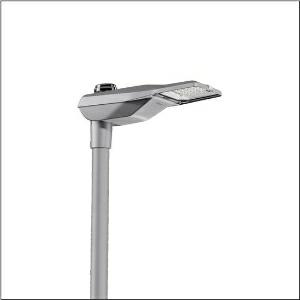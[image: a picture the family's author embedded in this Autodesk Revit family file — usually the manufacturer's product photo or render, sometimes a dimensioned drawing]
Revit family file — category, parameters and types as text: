
# Revit family: streetlight_sl_21_micro___st0_8a_5xe5c47n08cb_5e3b
name_source: partatom
category: Lighting Fixtures
units: mm (PartAtom-declared; Revit-internal decimal feet)

## family parameters
Cut with Voids When Loaded = No
Host = Face
Light Source = No
Part Type = Normal
Room Calculation Point = No
Round Connector Dimension = Use Diameter
Shared = No

## types (1)
- --- (1 x LED, 2380 lm, 15.8 W, 4000K)
    Apparent Load = 16 VA
    CIE Flux Codes = 38 75 97 100 100
    Color Rendering = 70
    Color Temperature = 4000K
    Default Elevation = 1800 mm
    Description = Streetlight SL 21 micro, mast luminaire, primary light control with lens, of PMMA, primary optical cover: cover, of toughened safety glass, transparent, light distribution: ST0.8a, light emission: direct distribution, primary light characteristic: asymmetric, installation type: post-top, LED, 3G 1.5mm², High Power LED, rated luminous flux: 2.380lm, luminous efficacy: 151lm/W, light colour: 740, colour temperature: 4000K, control gear: NEMA (7pin), control: overheat protection, pre-setting: linear dimming characteristic, constant luminous flux control, time-dependent luminous flux control, flexible luminous flux parameterisation, mains connection: 230..240V, AC, 50/60Hz, connection cable pre-assembled, cable length: 6,5m, wiring characteristics: H07RN-F, start of lifetime: 16W, end of service life: 16W, reduction: 8W, luminaire housing, of diecast aluminium (EN AC-44300), powder-coated, SITECO metallic grey (DB 702S), corrosivity category C5 high according to DIN EN ISO 12944, multi-level sealing system, sealing non-destructively replaceable, inclination adjustable: 0°, 5°, 10°, 15°, length: 528mm, width: 235mm, height: 110mm, spigot size: 76/60mm (post-top), mounting height: 4..8m, protection rating (complete): IP66, insulation class (complete): insulation class I (protective earthing), certification: CE, ENEC, ENEC+, VDE, impact resistance: IK10, permissible operating ambient temperature for outdoor applications: -40..+50°C, standard-compliant lighting for roads and squares, packaging unit: 1 piece

Light Distribution: ST0.8a
    Height = 110 mm
    Lamp = 1 x LED
    Lamp Light Flux = 2380 lm
    Lamp Power = 15.8 W
    Lamp count = 1
    Length = 528 mm
    Luminous efficacy = 151 lm/W
    Manufacturer = Siteco
    ModVariant = No
    Model = 5XE5C47N08CB
    Number of Poles = 1
    OnlyDefault = Yes
    Power Factor = 1
    Product Name = Streetlight SL 21 micro | ST0.8a
    Product group = mast luminaire | pylon top
    ProductGroupID = 6100
    Protection Class = Protection class I
    Protection Degree = IP 66
    RLX_Detail_Level = 1
    RLX_Emergency_Light_Flux = 0 lm
    RLX_Emergency_Type = 0
    RLX_Emergency_Type_DB = No
    RlxData = <blob elided: 98281 chars, md5=1947617e>
    Socket = socket
    Standby Power = 0 W
    System Light Flux = 2380 lm
    System Power = 16 W
    Type Comments = factory setting: luminous flux: 100 % | dim-lin: 254 | 300 mA
    Type Image = l_1294375.jpg
    URL = http://relux.com
    VarID = @adj_133837
    Voltage = 0 V
    Weight = 0.00 kg
    Width = 235 mm

## geometry (parser evidence)
native form markers: Blend x4, Sweep x9
no freeform markers — native parametric forms only
